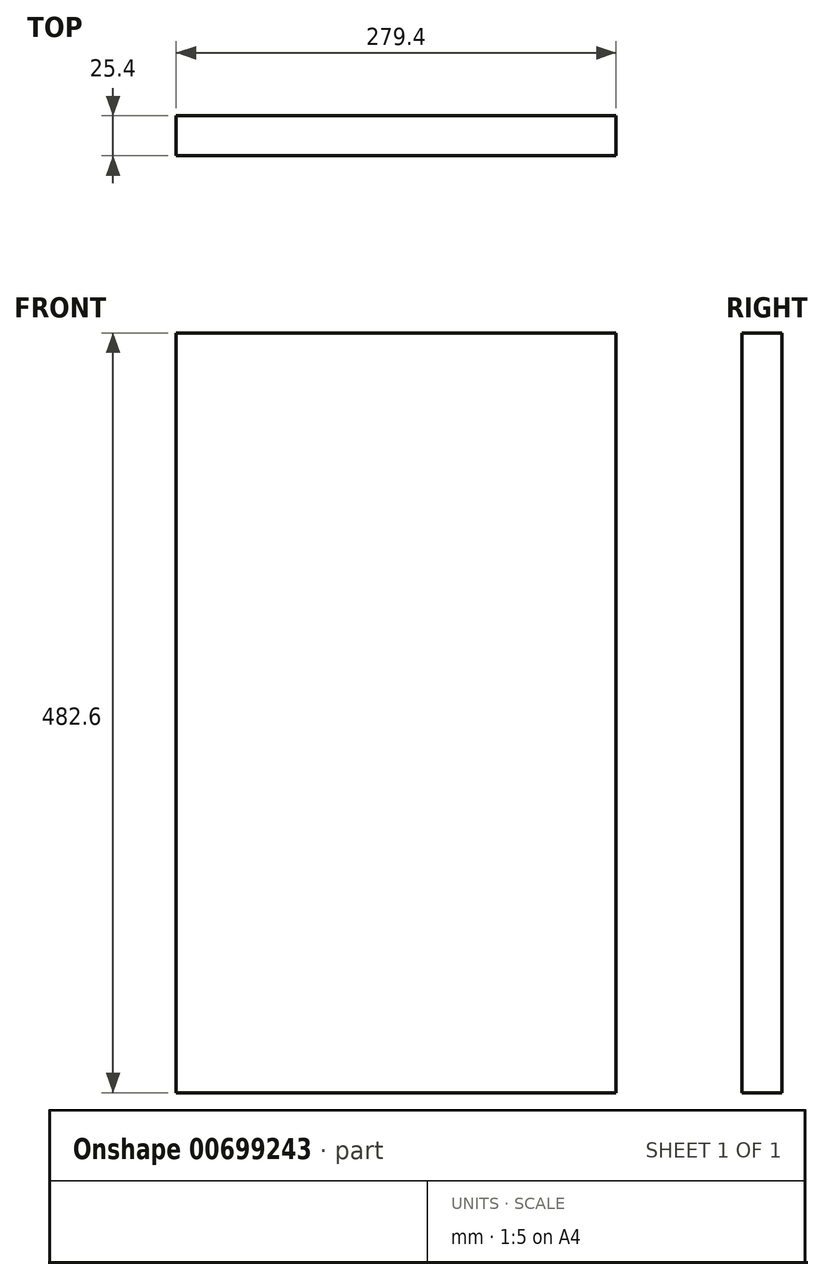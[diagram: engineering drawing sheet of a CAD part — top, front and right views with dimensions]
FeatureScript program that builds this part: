
annotation { "Feature Type Name" : "Feature", "Feature Type Description" : "" }
export const myFeature = defineFeature(function(context is Context, id is Id, definition is map)
    precondition{}
    {
        {
            var Q0;
            Q0=qCreatedBy(makeId("Front.planeOp"),FACE);
            var sketch = newSketch(context, id + "F0", { "sketchPlane" : qUnion([Q0])});
            skLineSegment(sketch, "E0.bottom", {"start": v(-139.7, 241.3) * mm, "end": v(139.7, 241.3) * mm});
            skLineSegment(sketch, "E0.top", {"start": v(-139.7, -241.3) * mm, "end": v(139.7, -241.3) * mm});
            skLineSegment(sketch, "E0.left", {"start": v(-139.7, 241.3) * mm, "end": v(-139.7, -241.3) * mm});
            skLineSegment(sketch, "E0.right", {"start": v(139.7, 241.3) * mm, "end": v(139.7, -241.3) * mm});
            skPoint(sketch, "E0.middle", {"position": v(0, 0) * mm});
            skSolve(sketch);
        }
        {
            var Q0;
            Q0=makeQuery(id+"F0.imprint","IMPRINT",FACE,{"disambiguationData":[TD([[makeQuery(id+"F0.imprint","IMPRINT",EDGE,{"derivedFrom":sQuery(id+"F0.wireOp",EDGE,"E0.bottom")}),-1.0]])]});
            extrude(context, id + "F1", {"entities" : qUnion([Q0]), "depth" : 25.4 * mm, "offsetDistance" : 25.4 * mm});
        }
    });
